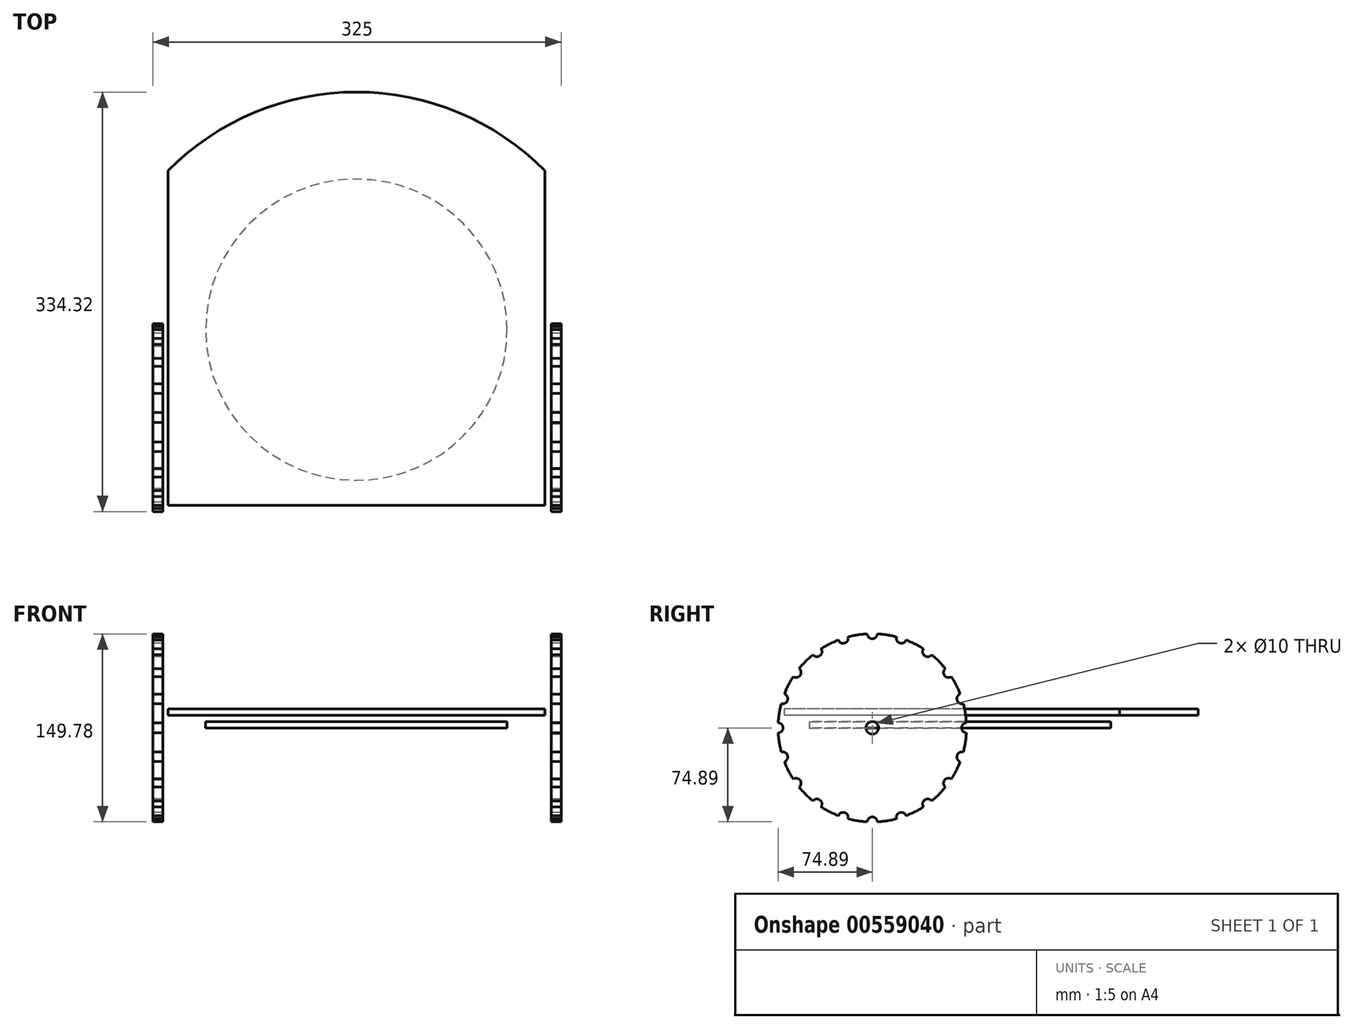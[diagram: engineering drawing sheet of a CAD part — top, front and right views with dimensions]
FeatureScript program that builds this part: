
annotation { "Feature Type Name" : "Feature", "Feature Type Description" : "" }
export const myFeature = defineFeature(function(context is Context, id is Id, definition is map)
    precondition{}
    {
        {
            var Q0;
            Q0=qCreatedBy(makeId("Top.planeOp"),FACE);
            var sketch = newSketch(context, id + "F0", { "sketchPlane" : qUnion([Q0])});
            skCircle(sketch, "E0", {"center": v(0, 0) * mm, "radius": 120 * mm});
            skLineSegment(sketch, "E1.filletArc", {"start": v(150, -145) * mm, "end": v(150, -145) * mm});
            skLineSegment(sketch, "E2", {"start": v(-150, 126.83) * mm, "end": v(150, 126.83) * mm});
            skArc(sketch, "E3", {"start": v(150, 126.83) * mm, "mid": v(0, 189.43) * mm, "end": v(-150, 126.83) * mm});
            skLineSegment(sketch, "E4.top", {"start": v(-150, -140) * mm, "end": v(150, -140) * mm});
            skLineSegment(sketch, "E4.left", {"start": v(-150, 126.83) * mm, "end": v(-150, -140) * mm});
            skLineSegment(sketch, "E4.right", {"start": v(150, 126.83) * mm, "end": v(150, -140) * mm});
            skSolve(sketch);
        }
        {
            var Q0;
            Q0=makeQuery(id+"F0.imprint","IMPRINT",FACE,{"disambiguationData":[TD([[makeQuery(id+"F0.imprint","IMPRINT",EDGE,{"derivedFrom":sQuery(id+"F0.wireOp",EDGE,"E0")}),1.0]])]});
            extrude(context, id + "F1", {"entities" : qUnion([Q0]), "depth" : 5 * mm, "offsetDistance" : 25 * mm});
        }
        {
            var Q0;
            Q0=makeQuery(id+"F0.imprint","IMPRINT",FACE,{"disambiguationData":[TD([[makeQuery(id+"F0.imprint","IMPRINT",EDGE,{"derivedFrom":sQuery(id+"F0.wireOp",EDGE,"E3")}),1.0]])]});
            var Q1;
            Q1=makeQuery(id+"F0.imprint","IMPRINT",FACE,{"disambiguationData":[TD([[makeQuery(id+"F0.imprint","IMPRINT",EDGE,{"derivedFrom":sQuery(id+"F0.wireOp",EDGE,"E0")}),-1.0]])]});
            var Q2;
            Q2=makeQuery(id+"F0.imprint","IMPRINT",FACE,{"disambiguationData":[TD([[makeQuery(id+"F0.imprint","IMPRINT",EDGE,{"derivedFrom":sQuery(id+"F0.wireOp",EDGE,"E0")}),1.0]])]});
            extrude(context, id + "F2", {"entities" : qUnion([Q0, Q1, Q2]), "depth" : 5 * mm, "offsetDistance" : 25 * mm});
        }
        {
            var Q0;
            Q0=makeQuery(id+"F2.opExtrude","SWEPT_BODY",BODY,{"disambiguationData":[OSD([sQuery(id+"F0.wireOp",EDGE,"E3"),sQuery(id+"F0.wireOp",EDGE,"E4.top"),sQuery(id+"F0.wireOp",EDGE,"E4.left"),sQuery(id+"F0.wireOp",EDGE,"E4.right")])]});
            transform(context, id + "F3", {"entities" : qUnion([Q0]), "transformType" : TransformType.TRANSLATION_3D, "dx" : 0 * mm, "dy" : 0 * mm, "dz" : 10 * mm, "makeCopy" : false});
        }
        {
            var Q0;
            Q0=qCreatedBy(makeId("Right.planeOp"),FACE);
            var sketch = newSketch(context, id + "F4", { "sketchPlane" : qUnion([Q0])});
            skCircle(sketch, "E5", {"center": v(0, 0) * mm, "radius": 75 * mm});
            skCircle(sketch, "E6", {"center": v(0, 75) * mm, "radius": 4 * mm});
            skCircle(sketch, "E7.1.0", {"center": v(-23.18, 71.33) * mm, "radius": 4 * mm});
            skCircle(sketch, "E7.2.0", {"center": v(-44.08, 60.68) * mm, "radius": 4 * mm});
            skCircle(sketch, "E7.3.0", {"center": v(-60.68, 44.08) * mm, "radius": 4 * mm});
            skCircle(sketch, "E7.4.0", {"center": v(-71.33, 23.18) * mm, "radius": 4 * mm});
            skCircle(sketch, "E7.5.0", {"center": v(-75, 0) * mm, "radius": 4 * mm});
            skCircle(sketch, "E7.6.0", {"center": v(-71.33, -23.18) * mm, "radius": 4 * mm});
            skCircle(sketch, "E7.7.0", {"center": v(-60.68, -44.08) * mm, "radius": 4 * mm});
            skCircle(sketch, "E7.8.0", {"center": v(-44.08, -60.68) * mm, "radius": 4 * mm});
            skCircle(sketch, "E7.9.0", {"center": v(-23.18, -71.33) * mm, "radius": 4 * mm});
            skCircle(sketch, "E7.10.0", {"center": v(0, -75) * mm, "radius": 4 * mm});
            skCircle(sketch, "E7.11.0", {"center": v(23.18, -71.33) * mm, "radius": 4 * mm});
            skCircle(sketch, "E7.12.0", {"center": v(44.08, -60.68) * mm, "radius": 4 * mm});
            skCircle(sketch, "E7.13.0", {"center": v(60.68, -44.08) * mm, "radius": 4 * mm});
            skCircle(sketch, "E7.14.0", {"center": v(71.33, -23.18) * mm, "radius": 4 * mm});
            skCircle(sketch, "E7.15.0", {"center": v(75, 0) * mm, "radius": 4 * mm});
            skCircle(sketch, "E7.16.0", {"center": v(71.33, 23.18) * mm, "radius": 4 * mm});
            skCircle(sketch, "E7.17.0", {"center": v(60.68, 44.08) * mm, "radius": 4 * mm});
            skCircle(sketch, "E7.18.0", {"center": v(44.08, 60.68) * mm, "radius": 4 * mm});
            skCircle(sketch, "E7.19.0", {"center": v(23.18, 71.33) * mm, "radius": 4 * mm});
            skSolve(sketch);
        }
        {
            var Q0;
            {var subQ0=sQuery(id+"F4.wireOp",EDGE,"E5");var subQ40=sQuery(id+"F4.wireOp",EDGE,"E6");var subQ41=makeQuery(id+"F4.imprint","INTERSECT",VERTEX,{"disambiguationData":[OD(0.0)],"derivedFrom":[subQ40,subQ0]});Q0=makeQuery(id+"F4.imprint","IMPRINT",FACE,{"disambiguationData":[TD([[makeQuery(id+"F4.imprint","IMPRINT",EDGE,{"disambiguationData":[TD([[subQ41,1.0]])],"derivedFrom":subQ40}),-1.0]])]});}
            extrude(context, id + "F5", {"entities" : qUnion([Q0]), "depth" : 8 * mm, "offsetDistance" : 25 * mm});
        }
        {
            var Q0;
            Q0=makeQuery(id+"F5.opExtrude","SWEPT_BODY",BODY,{"disambiguationData":[OSD([sQuery(id+"F4.wireOp",EDGE,"E6"),sQuery(id+"F4.wireOp",EDGE,"E7.1.0"),sQuery(id+"F4.wireOp",EDGE,"E7.2.0"),sQuery(id+"F4.wireOp",EDGE,"E7.3.0"),sQuery(id+"F4.wireOp",EDGE,"E7.4.0"),sQuery(id+"F4.wireOp",EDGE,"E7.5.0"),sQuery(id+"F4.wireOp",EDGE,"E7.6.0"),sQuery(id+"F4.wireOp",EDGE,"E7.7.0"),sQuery(id+"F4.wireOp",EDGE,"E7.8.0"),sQuery(id+"F4.wireOp",EDGE,"E7.9.0"),sQuery(id+"F4.wireOp",EDGE,"E7.10.0"),sQuery(id+"F4.wireOp",EDGE,"E7.11.0"),sQuery(id+"F4.wireOp",EDGE,"E7.12.0"),sQuery(id+"F4.wireOp",EDGE,"E7.13.0"),sQuery(id+"F4.wireOp",EDGE,"E7.14.0"),sQuery(id+"F4.wireOp",EDGE,"E7.15.0"),sQuery(id+"F4.wireOp",EDGE,"E7.16.0"),sQuery(id+"F4.wireOp",EDGE,"E7.17.0"),sQuery(id+"F4.wireOp",EDGE,"E7.18.0"),sQuery(id+"F4.wireOp",EDGE,"E7.19.0"),sQuery(id+"F4.wireOp",EDGE,"E5")])]});
            transform(context, id + "F6", {"entities" : qUnion([Q0]), "transformType" : TransformType.TRANSLATION_3D, "dx" : 155 * mm, "dy" : 0 * mm, "dz" : 0 * mm, "makeCopy" : false});
        }
        {
            var Q0;
            Q0=makeQuery(id+"F5.opExtrude","SWEPT_BODY",BODY,{"disambiguationData":[OSD([sQuery(id+"F4.wireOp",EDGE,"E6"),sQuery(id+"F4.wireOp",EDGE,"E7.1.0"),sQuery(id+"F4.wireOp",EDGE,"E7.2.0"),sQuery(id+"F4.wireOp",EDGE,"E7.3.0"),sQuery(id+"F4.wireOp",EDGE,"E7.4.0"),sQuery(id+"F4.wireOp",EDGE,"E7.5.0"),sQuery(id+"F4.wireOp",EDGE,"E7.6.0"),sQuery(id+"F4.wireOp",EDGE,"E7.7.0"),sQuery(id+"F4.wireOp",EDGE,"E7.8.0"),sQuery(id+"F4.wireOp",EDGE,"E7.9.0"),sQuery(id+"F4.wireOp",EDGE,"E7.10.0"),sQuery(id+"F4.wireOp",EDGE,"E7.11.0"),sQuery(id+"F4.wireOp",EDGE,"E7.12.0"),sQuery(id+"F4.wireOp",EDGE,"E7.13.0"),sQuery(id+"F4.wireOp",EDGE,"E7.14.0"),sQuery(id+"F4.wireOp",EDGE,"E7.15.0"),sQuery(id+"F4.wireOp",EDGE,"E7.16.0"),sQuery(id+"F4.wireOp",EDGE,"E7.17.0"),sQuery(id+"F4.wireOp",EDGE,"E7.18.0"),sQuery(id+"F4.wireOp",EDGE,"E7.19.0"),sQuery(id+"F4.wireOp",EDGE,"E5")])]});
            var Q1;
            Q1=makeQuery(id+"F2.opExtrude","CAP_EDGE",EDGE,{"disambiguationData":[OSD([sQuery(id+"F0.wireOp",EDGE,"E4.right")])],"isStart":false});
            var Q2;
            Q2=makeQuery(id+"F2.opExtrude","CAP_EDGE",EDGE,{"disambiguationData":[OSD([sQuery(id+"F0.wireOp",EDGE,"E4.left")])],"isStart":false});
            transform(context, id + "F7", {"entities" : qUnion([Q0]), "transformType" : TransformType.TRANSLATION_3D, "dx" : 0 * mm, "dy" : -70 * mm, "dz" : 0 * mm, "makeCopy" : false});
        }
        {
            var Q0;
            Q0=makeQuery(id+"F5.opExtrude","SWEPT_BODY",BODY,{"disambiguationData":[OSD([sQuery(id+"F4.wireOp",EDGE,"E6"),sQuery(id+"F4.wireOp",EDGE,"E7.1.0"),sQuery(id+"F4.wireOp",EDGE,"E7.2.0"),sQuery(id+"F4.wireOp",EDGE,"E7.3.0"),sQuery(id+"F4.wireOp",EDGE,"E7.4.0"),sQuery(id+"F4.wireOp",EDGE,"E7.5.0"),sQuery(id+"F4.wireOp",EDGE,"E7.6.0"),sQuery(id+"F4.wireOp",EDGE,"E7.7.0"),sQuery(id+"F4.wireOp",EDGE,"E7.8.0"),sQuery(id+"F4.wireOp",EDGE,"E7.9.0"),sQuery(id+"F4.wireOp",EDGE,"E7.10.0"),sQuery(id+"F4.wireOp",EDGE,"E7.11.0"),sQuery(id+"F4.wireOp",EDGE,"E7.12.0"),sQuery(id+"F4.wireOp",EDGE,"E7.13.0"),sQuery(id+"F4.wireOp",EDGE,"E7.14.0"),sQuery(id+"F4.wireOp",EDGE,"E7.15.0"),sQuery(id+"F4.wireOp",EDGE,"E7.16.0"),sQuery(id+"F4.wireOp",EDGE,"E7.17.0"),sQuery(id+"F4.wireOp",EDGE,"E7.18.0"),sQuery(id+"F4.wireOp",EDGE,"E7.19.0"),sQuery(id+"F4.wireOp",EDGE,"E5")])]});
            transform(context, id + "F8", {"entities" : qUnion([Q0]), "transformType" : TransformType.COPY});
        }
        {
            var Q0;
            Q0=makeQuery(id+"F5.opExtrude","SWEPT_BODY",BODY,{"disambiguationData":[OSD([sQuery(id+"F4.wireOp",EDGE,"E6"),sQuery(id+"F4.wireOp",EDGE,"E7.1.0"),sQuery(id+"F4.wireOp",EDGE,"E7.2.0"),sQuery(id+"F4.wireOp",EDGE,"E7.3.0"),sQuery(id+"F4.wireOp",EDGE,"E7.4.0"),sQuery(id+"F4.wireOp",EDGE,"E7.5.0"),sQuery(id+"F4.wireOp",EDGE,"E7.6.0"),sQuery(id+"F4.wireOp",EDGE,"E7.7.0"),sQuery(id+"F4.wireOp",EDGE,"E7.8.0"),sQuery(id+"F4.wireOp",EDGE,"E7.9.0"),sQuery(id+"F4.wireOp",EDGE,"E7.10.0"),sQuery(id+"F4.wireOp",EDGE,"E7.11.0"),sQuery(id+"F4.wireOp",EDGE,"E7.12.0"),sQuery(id+"F4.wireOp",EDGE,"E7.13.0"),sQuery(id+"F4.wireOp",EDGE,"E7.14.0"),sQuery(id+"F4.wireOp",EDGE,"E7.15.0"),sQuery(id+"F4.wireOp",EDGE,"E7.16.0"),sQuery(id+"F4.wireOp",EDGE,"E7.17.0"),sQuery(id+"F4.wireOp",EDGE,"E7.18.0"),sQuery(id+"F4.wireOp",EDGE,"E7.19.0"),sQuery(id+"F4.wireOp",EDGE,"E5")])]});
            transform(context, id + "F9", {"entities" : qUnion([Q0]), "transformType" : TransformType.TRANSLATION_3D, "dx" : -317 * mm, "dy" : 0 * mm, "dz" : 0 * mm, "makeCopy" : true});
        }
        {
            var Q0;
            Q0=makeQuery(id+"F5.opExtrude","CAP_FACE",FACE,{"disambiguationData":[OSD([sQuery(id+"F4.wireOp",EDGE,"E6"),sQuery(id+"F4.wireOp",EDGE,"E7.1.0"),sQuery(id+"F4.wireOp",EDGE,"E7.2.0"),sQuery(id+"F4.wireOp",EDGE,"E7.3.0"),sQuery(id+"F4.wireOp",EDGE,"E7.4.0"),sQuery(id+"F4.wireOp",EDGE,"E7.5.0"),sQuery(id+"F4.wireOp",EDGE,"E7.6.0"),sQuery(id+"F4.wireOp",EDGE,"E7.7.0"),sQuery(id+"F4.wireOp",EDGE,"E7.8.0"),sQuery(id+"F4.wireOp",EDGE,"E7.9.0"),sQuery(id+"F4.wireOp",EDGE,"E7.10.0"),sQuery(id+"F4.wireOp",EDGE,"E7.11.0"),sQuery(id+"F4.wireOp",EDGE,"E7.12.0"),sQuery(id+"F4.wireOp",EDGE,"E7.13.0"),sQuery(id+"F4.wireOp",EDGE,"E7.14.0"),sQuery(id+"F4.wireOp",EDGE,"E7.15.0"),sQuery(id+"F4.wireOp",EDGE,"E7.16.0"),sQuery(id+"F4.wireOp",EDGE,"E7.17.0"),sQuery(id+"F4.wireOp",EDGE,"E7.18.0"),sQuery(id+"F4.wireOp",EDGE,"E7.19.0"),sQuery(id+"F4.wireOp",EDGE,"E5")])],"isStart":false});
            var sketch = newSketch(context, id + "F10", { "sketchPlane" : qUnion([Q0])});
            skCircle(sketch, "E8", {"center": v(-70, 0) * mm, "radius": 5 * mm});
            skSolve(sketch);
        }
        {
            var Q0;
            Q0=makeQuery(id+"F10.imprint","IMPRINT",FACE,{"disambiguationData":[TD([[makeQuery(id+"F10.imprint","IMPRINT",EDGE,{"derivedFrom":sQuery(id+"F10.wireOp",EDGE,"E8")}),1.0]])]});
            extrude(context, id + "F11", {"entities" : qUnion([Q0]), "operationType" : NewBodyOperationType.REMOVE, "oppositeDirection" : true, "depth" : 25 * mm, "offsetDistance" : 25 * mm});
        }
    });
